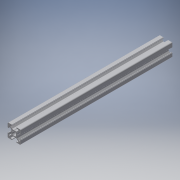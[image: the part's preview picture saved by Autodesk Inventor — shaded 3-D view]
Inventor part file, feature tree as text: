
AUTODESK INVENTOR PART (.ipt)
format: ipt  version: 2016 (Build 200138000, 138)  size: 392,192 bytes
history: native  units: in
note: dims shown in document units (in); Inventor stores cm internally (conversion verified against a paired STEP export)
features: other x5, sketch x1
ambient origin geometry x8: Origin, YZ Plane, XZ Plane, XY Plane, X Axis, Y Axis, Z Axis, Center Point
bodies: Solid1 (feature_tree)
feature tree (6):
  other  "Bosch 20x20 9 in actual.ipt"
  other  "Blocks"
  other  "20x20"
  other  "Solid1::Bosch 20x20 9 in actual.ipt"
  other  "TaggingFeature1"
  sketch  "Sketch1"  dims[d0=0.3937in]
